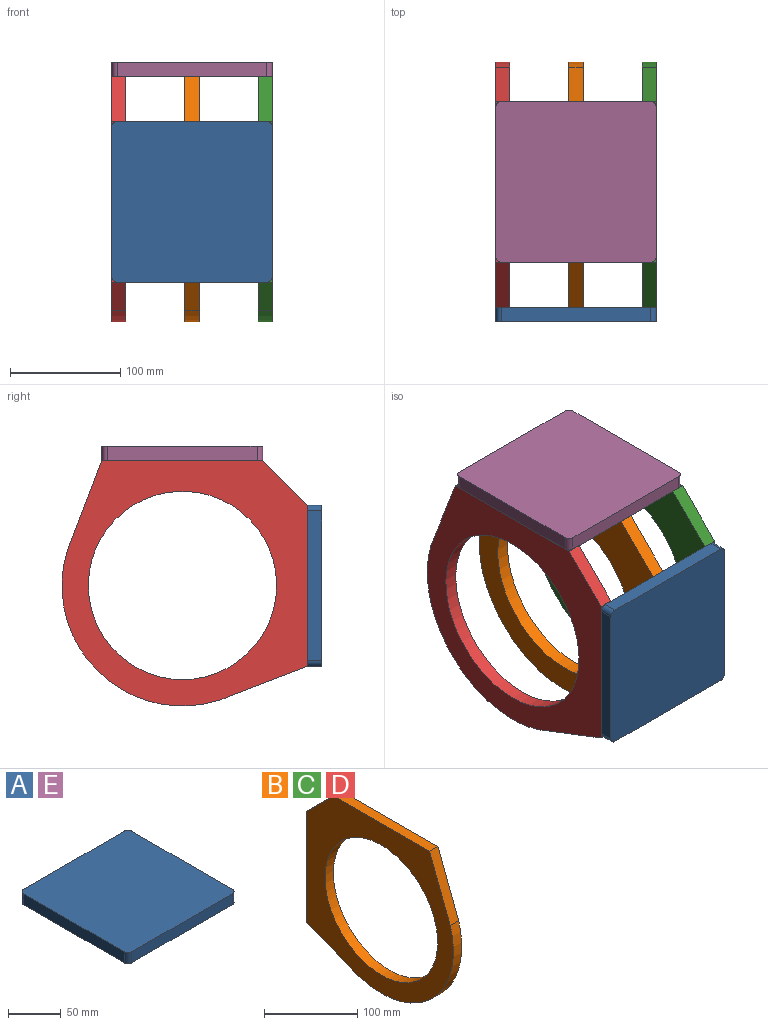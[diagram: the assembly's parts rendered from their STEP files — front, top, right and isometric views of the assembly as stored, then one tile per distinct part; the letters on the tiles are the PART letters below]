
ASSEMBLY  parts=5 mates=4
PART A: 10 faces, bbox 145.6x145.6x12.7 mm
  f0: plane 135.61x12.7mm, normal (-1,0,0), area 1722.2mm2, adj f1,f7,f8,f9
  f1: cylinder r=5mm len=12.7mm, axis (0,0,-1), area 99.7mm2, adj f0,f2,f8,f9
  f2: plane 135.61x12.7mm, normal (0,-1,0), area 1722.2mm2, adj f1,f3,f8,f9
  f3: cylinder r=5mm len=12.7mm, axis (0,0,-1), area 99.7mm2, adj f2,f4,f8,f9
  f4: plane 135.61x12.7mm, normal (1,0,0), area 1722.2mm2, adj f3,f5,f8,f9
  f5: cylinder r=5mm len=12.7mm, axis (0,0,-1), area 99.7mm2, adj f4,f6,f8,f9
  f6: plane 135.61x12.7mm, normal (0,1,0), area 1722.2mm2, adj f5,f7,f8,f9
  f7: cylinder r=5mm len=12.7mm, axis (0,0,-1), area 99.7mm2, adj f0,f6,f8,f9
  f8: plane 145.61x145.61mm, normal (0,0,1), area 21180.8mm2, adj f0,f1,f2,f3,f4,f5,f6,f7
  f9: plane 145.61x145.61mm, normal (0,0,-1), area 21180.8mm2, adj f0,f1,f2,f3,f4,f5,f6,f7
PART B: 9 faces, bbox 12.7x222.7x222.7 mm
  f0: plane 145.61x12.7mm, normal (0,0,1), area 1849.2mm2, adj f1,f5,f7,f8
  f1: plane 81.64x31.34mm, normal (0,-0.93,0.36), area 1110.6mm2, adj f0,f2,f7,f8
  f2: cylinder r=109.18mm len=155.32mm, axis (-1,0,0), area 3194.4mm2, adj f1,f3,f7,f8
  f3: plane 67.42x25.88mm, normal (0,0.36,-0.93), area 917.2mm2, adj f2,f4,f7,f8
  f4: plane 145.61x12.7mm, normal (0,1,0), area 1849.2mm2, adj f3,f5,f7,f8
  f5: plane 41.02x41.02mm, normal (0,0.71,0.71), area 736.8mm2, adj f0,f4,f7,f8
  f6: cylinder r=85.33mm len=170.66mm, axis (-1,0,0), area 6808.8mm2, adj f7,f8
  f7: plane 222.74x222.74mm, normal (1,0,0), area 19905.8mm2, adj f0,f1,f2,f3,f4,f5,f6
  f8: plane 222.74x222.74mm, normal (-1,0,0), area 19905.8mm2, adj f0,f1,f2,f3,f4,f5,f6
PART C: same geometry as B
PART D: same geometry as B
PART E: same geometry as A
PLACE A rot(axis=(1,0,0),90deg) t=(0,-113.83,-113.83)mm
PLACE B rot(axis=(0,0,1),180deg) t=(6.35,-0.26,-113.56)mm
PLACE C rot(axis=(0,0,1),180deg) t=(72.81,-0.26,-113.56)mm
PLACE D rot(axis=(0,0,1),180deg) t=(-60.11,-0.26,-113.56)mm
PLACE E at identity fixed
MATE fastened B.f4 <-> A.f9  axis (0,-1,0) through (0,-113.83,-41.02)mm
MATE fastened C.f0 <-> E.f9  axis (0,0,1) through (72.81,0,0)mm
MATE fastened B.f0 <-> E.f9  axis (0,0,1) through (0,0,0)mm
MATE fastened D.f0 <-> E.f9  axis (0,0,1) through (-72.81,0,0)mm
